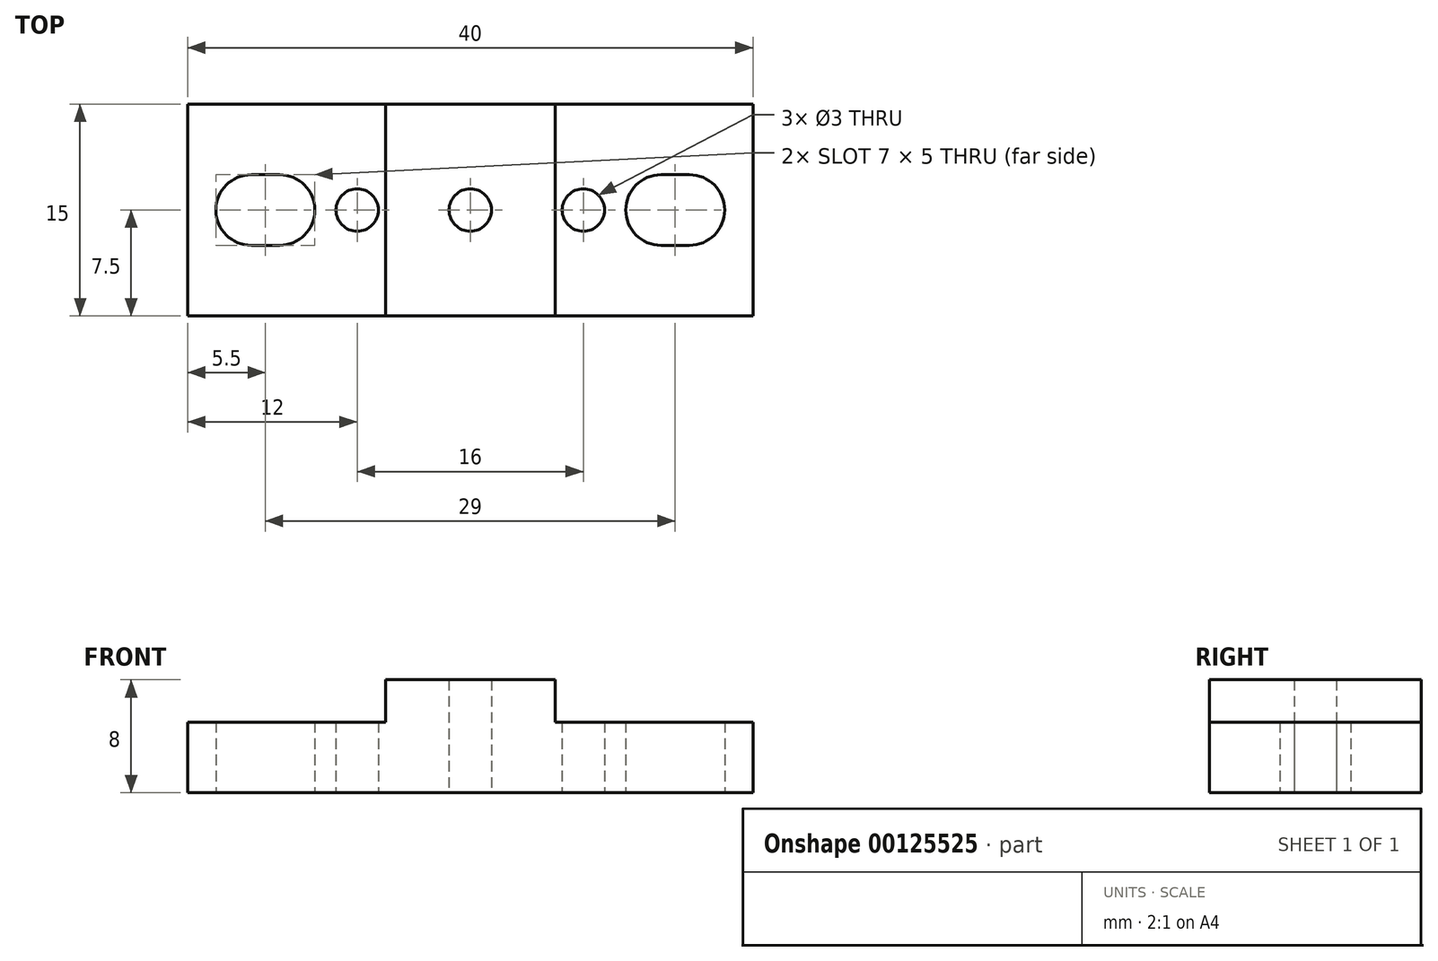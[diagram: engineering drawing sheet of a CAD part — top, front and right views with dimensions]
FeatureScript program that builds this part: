
annotation { "Feature Type Name" : "Feature", "Feature Type Description" : "" }
export const myFeature = defineFeature(function(context is Context, id is Id, definition is map)
    precondition{}
    {
        {
            var Q0;
            Q0=qCreatedBy(makeId("Top.planeOp"),FACE);
            var sketch = newSketch(context, id + "F0", { "sketchPlane" : qUnion([Q0])});
            skLineSegment(sketch, "E0.bottom", {"start": v(-20, 7.5) * mm, "end": v(20, 7.5) * mm});
            skLineSegment(sketch, "E0.top", {"start": v(-20, -7.5) * mm, "end": v(20, -7.5) * mm});
            skLineSegment(sketch, "E0.left", {"start": v(-20, 7.5) * mm, "end": v(-20, -7.5) * mm});
            skLineSegment(sketch, "E0.right", {"start": v(20, 7.5) * mm, "end": v(20, -7.5) * mm});
            skPoint(sketch, "E0.middle", {"position": v(0, 0) * mm});
            skCircle(sketch, "E1", {"center": v(0, 0) * mm, "radius": 1.5 * mm});
            skCircle(sketch, "E2", {"center": v(-15.5, 0) * mm, "radius": 2.5 * mm});
            skCircle(sketch, "E3", {"center": v(15.5, 0) * mm, "radius": 2.5 * mm});
            skLineSegment(sketch, "E4", {"start": v(-6, 7.5) * mm, "end": v(-6, -7.5) * mm});
            skLineSegment(sketch, "E5", {"start": v(6, 7.5) * mm, "end": v(6, -7.5) * mm});
            skCircle(sketch, "E6", {"center": v(-8, 0) * mm, "radius": 1.5 * mm});
            skCircle(sketch, "E7", {"center": v(8, 0) * mm, "radius": 1.5 * mm});
            skPoint(sketch, "E7.centerSnap0", {"position": v(6, 0) * mm});
            skCircle(sketch, "E8", {"center": v(-13.5, 0) * mm, "radius": 2.5 * mm});
            skCircle(sketch, "E9", {"center": v(13.5, 0) * mm, "radius": 2.5 * mm});
            skLineSegment(sketch, "E10", {"start": v(-15.5, 2.5) * mm, "end": v(-13.5, 2.5) * mm});
            skLineSegment(sketch, "E11", {"start": v(-15.5, -2.5) * mm, "end": v(-13.5, -2.5) * mm});
            skLineSegment(sketch, "E12", {"start": v(13.5, 2.5) * mm, "end": v(15.5, 2.5) * mm});
            skLineSegment(sketch, "E13", {"start": v(13.5, -2.5) * mm, "end": v(15.5, -2.5) * mm});
            skCircle(sketch, "E14", {"center": v(-13.5, 0) * mm, "radius": 3.5 * mm, "construction": true});
            skSolve(sketch);
        }
        {
            var Q0;
            Q0=makeQuery(id+"F0.imprint","IMPRINT",FACE,{"disambiguationData":[TD([[makeQuery(id+"F0.imprint","IMPRINT",EDGE,{"derivedFrom":sQuery(id+"F0.wireOp",EDGE,"E0.bottom")}),-1.0]])]});
            var Q1;
            {var subQ3=sQuery(id+"F0.wireOp",EDGE,"E0.left");Q1=makeQuery(id+"F0.imprint","IMPRINT",FACE,{"disambiguationData":[TD([[makeQuery(id+"F0.imprint","IMPRINT",EDGE,{"derivedFrom":subQ3}),1.0]])]});}
            var Q2;
            {var subQ0=sQuery(id+"F0.wireOp",EDGE,"E0.right");Q2=makeQuery(id+"F0.imprint","IMPRINT",FACE,{"disambiguationData":[TD([[makeQuery(id+"F0.imprint","IMPRINT",EDGE,{"derivedFrom":subQ0}),-1.0]])]});}
            extrude(context, id + "F1", {"entities" : qUnion([Q0, Q1, Q2]), "depth" : 5 * mm});
        }
        {
            var Q0;
            Q0=makeQuery(id+"F0.imprint","IMPRINT",FACE,{"disambiguationData":[TD([[makeQuery(id+"F0.imprint","IMPRINT",EDGE,{"derivedFrom":sQuery(id+"F0.wireOp",EDGE,"E1")}),-1.0]])]});
            extrude(context, id + "F2", {"entities" : qUnion([Q0]), "operationType" : NewBodyOperationType.ADD, "depth" : 8 * mm});
        }
    });
